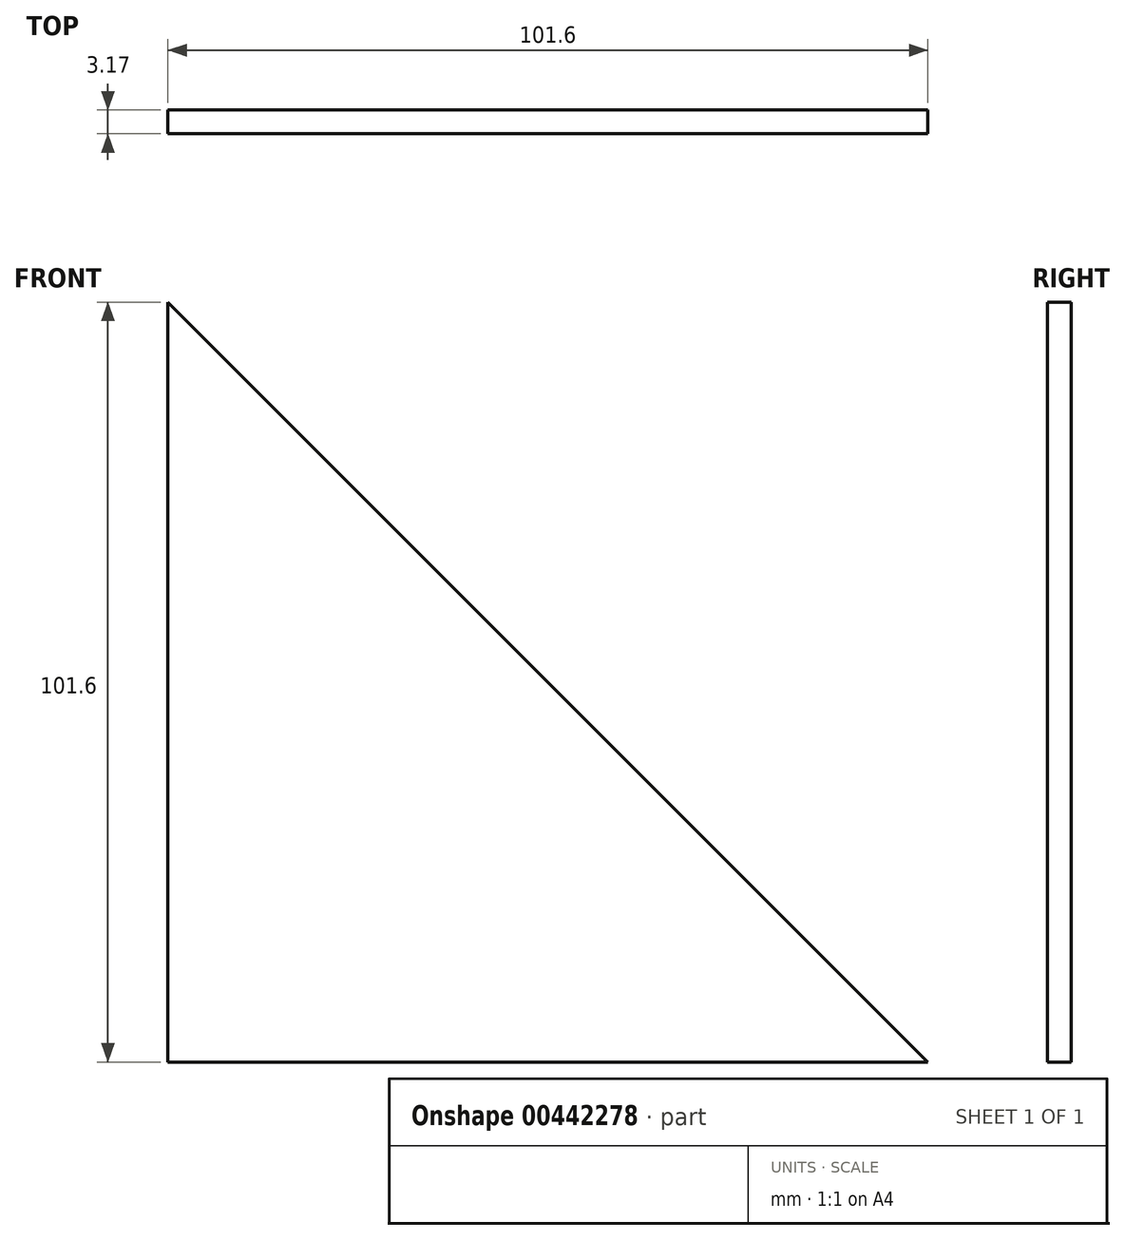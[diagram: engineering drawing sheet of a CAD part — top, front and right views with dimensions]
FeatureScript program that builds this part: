
annotation { "Feature Type Name" : "Feature", "Feature Type Description" : "" }
export const myFeature = defineFeature(function(context is Context, id is Id, definition is map)
    precondition{}
    {
        {
            var Q0;
            Q0=qCreatedBy(makeId("Front.planeOp"),FACE);
            var sketch = newSketch(context, id + "F0", { "sketchPlane" : qUnion([Q0])});
            skLineSegment(sketch, "E0", {"start": v(0, 0) * mm, "end": v(0, 101.6) * mm});
            skLineSegment(sketch, "E1", {"start": v(0, 101.6) * mm, "end": v(101.6, 0) * mm});
            skLineSegment(sketch, "E2", {"start": v(101.6, 0) * mm, "end": v(0, 0) * mm});
            skSolve(sketch);
        }
        {
            var Q0;
            Q0=makeQuery(id+"F0.imprint","IMPRINT",FACE,{"disambiguationData":[TD([[makeQuery(id+"F0.imprint","IMPRINT",EDGE,{"derivedFrom":sQuery(id+"F0.wireOp",EDGE,"E0")}),-1.0]])]});
            extrude(context, id + "F1", {"entities" : qUnion([Q0]), "depth" : 3.17 * mm});
        }
    });
